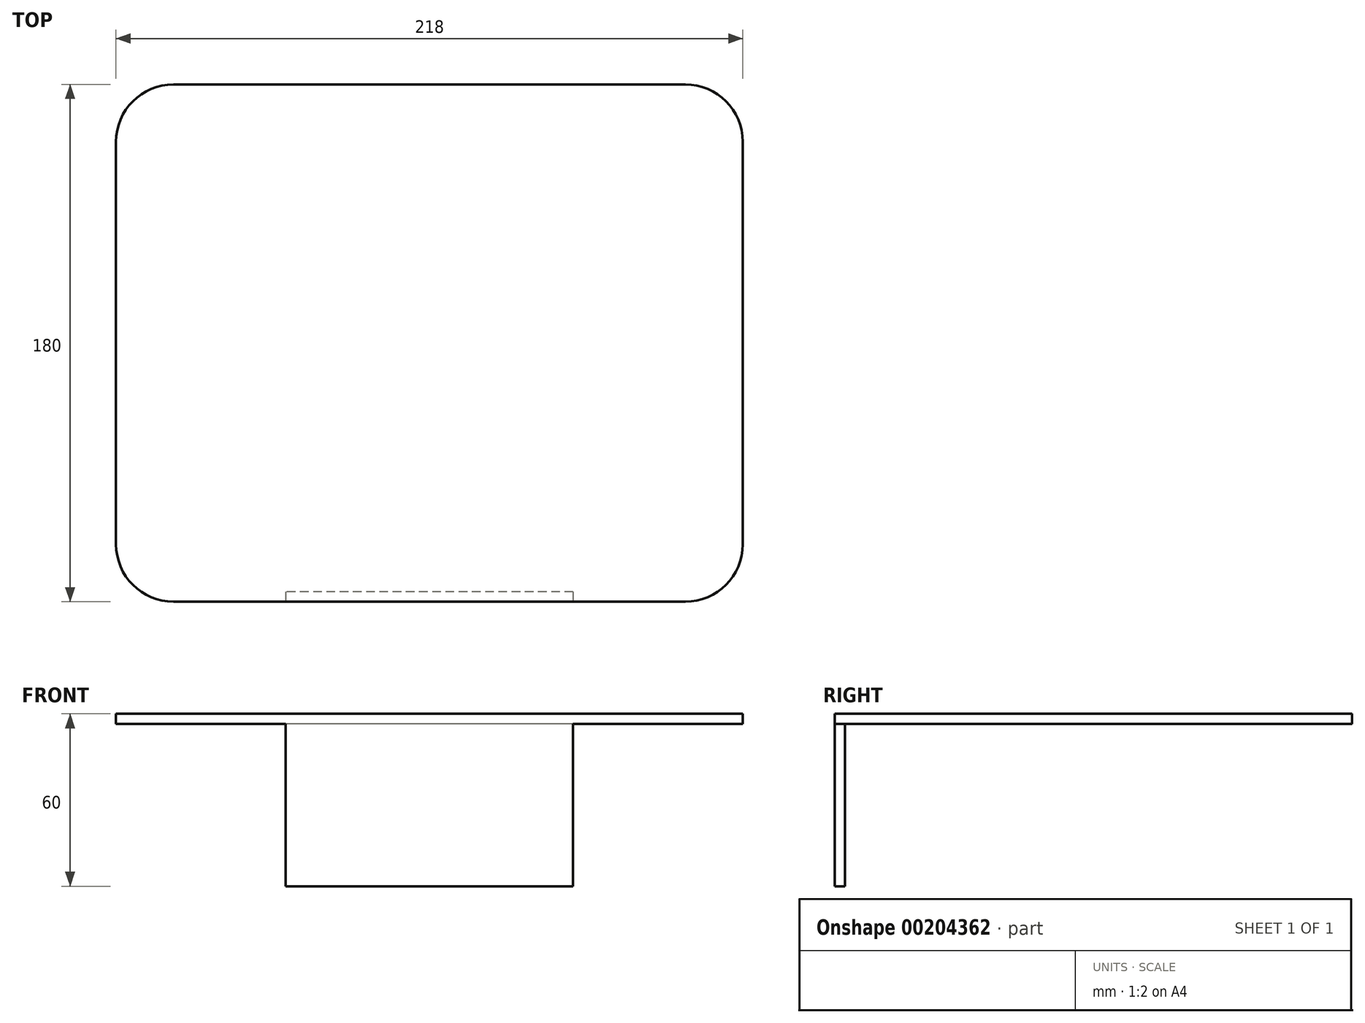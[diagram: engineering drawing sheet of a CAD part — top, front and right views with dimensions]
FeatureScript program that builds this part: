
annotation { "Feature Type Name" : "Feature", "Feature Type Description" : "" }
export const myFeature = defineFeature(function(context is Context, id is Id, definition is map)
    precondition{}
    {
        {
            var Q0;
            Q0=qCreatedBy(makeId("Right.planeOp"),FACE);
            var sketch = newSketch(context, id + "F0", { "sketchPlane" : qUnion([Q0])});
            skLineSegment(sketch, "E0", {"start": v(-415.42, -414.48) * mm, "end": v(-415.42, -354.48) * mm});
            skLineSegment(sketch, "E1", {"start": v(-415.42, -354.48) * mm, "end": v(-235.42, -354.48) * mm});
            skLineSegment(sketch, "E2", {"start": v(-235.42, -354.48) * mm, "end": v(-235.42, -357.98) * mm});
            skLineSegment(sketch, "E3", {"start": v(-235.42, -357.98) * mm, "end": v(-411.92, -357.98) * mm});
            skLineSegment(sketch, "E4", {"start": v(-411.92, -357.98) * mm, "end": v(-411.92, -414.48) * mm});
            skLineSegment(sketch, "E5", {"start": v(-411.92, -414.48) * mm, "end": v(-415.42, -414.48) * mm});
            skLineSegment(sketch, "E6", {"start": v(-411.92, -357.98) * mm, "end": v(-415.42, -357.98) * mm});
            skSolve(sketch);
        }
        {
            var Q0;
            {var subQ0=sQuery(id+"F0.wireOp",EDGE,"E1");Q0=makeQuery(id+"F0.imprint","IMPRINT",FACE,{"disambiguationData":[TD([[makeQuery(id+"F0.imprint","IMPRINT",EDGE,{"derivedFrom":subQ0}),-1.0]])]});}
            extrude(context, id + "F1", {"entities" : qUnion([Q0]), "endBound" : BoundingType.SYMMETRIC, "depth" : 218 * mm});
        }
        {
            var Q0;
            Q0 = qSketchRegion(id + "F0", true);
            extrude(context, id + "F2", {"entities" : qUnion([Q0]), "operationType" : NewBodyOperationType.ADD, "endBound" : BoundingType.SYMMETRIC, "depth" : 100 * mm});
        }
        {
            var Q0;
            Q0=makeQuery(id+"F1.opExtrude","CAP_EDGE",EDGE,{"disambiguationData":[OSD([sQuery(id+"F0.wireOp",EDGE,"E2")])],"isStart":false});
            var Q1;
            Q1=makeQuery(id+"F1.opExtrude","CAP_EDGE",EDGE,{"disambiguationData":[OSD([sQuery(id+"F0.wireOp",EDGE,"E2")])],"isStart":true});
            var Q2;
            Q2=makeQuery(id+"F1.opExtrude","CAP_EDGE",EDGE,{"disambiguationData":[OSD([sQuery(id+"F0.wireOp",EDGE,"E0")])],"isStart":true});
            var Q3;
            Q3=makeQuery(id+"F1.opExtrude","CAP_EDGE",EDGE,{"disambiguationData":[OSD([sQuery(id+"F0.wireOp",EDGE,"E0")])],"isStart":false});
            fillet(context, id + "F3", {"entities" : qUnion([Q0, Q1, Q2, Q3]), "radius" : 20 * mm, "tangentPropagation" : true, "allowEdgeOverflow" : false});
        }
    });
